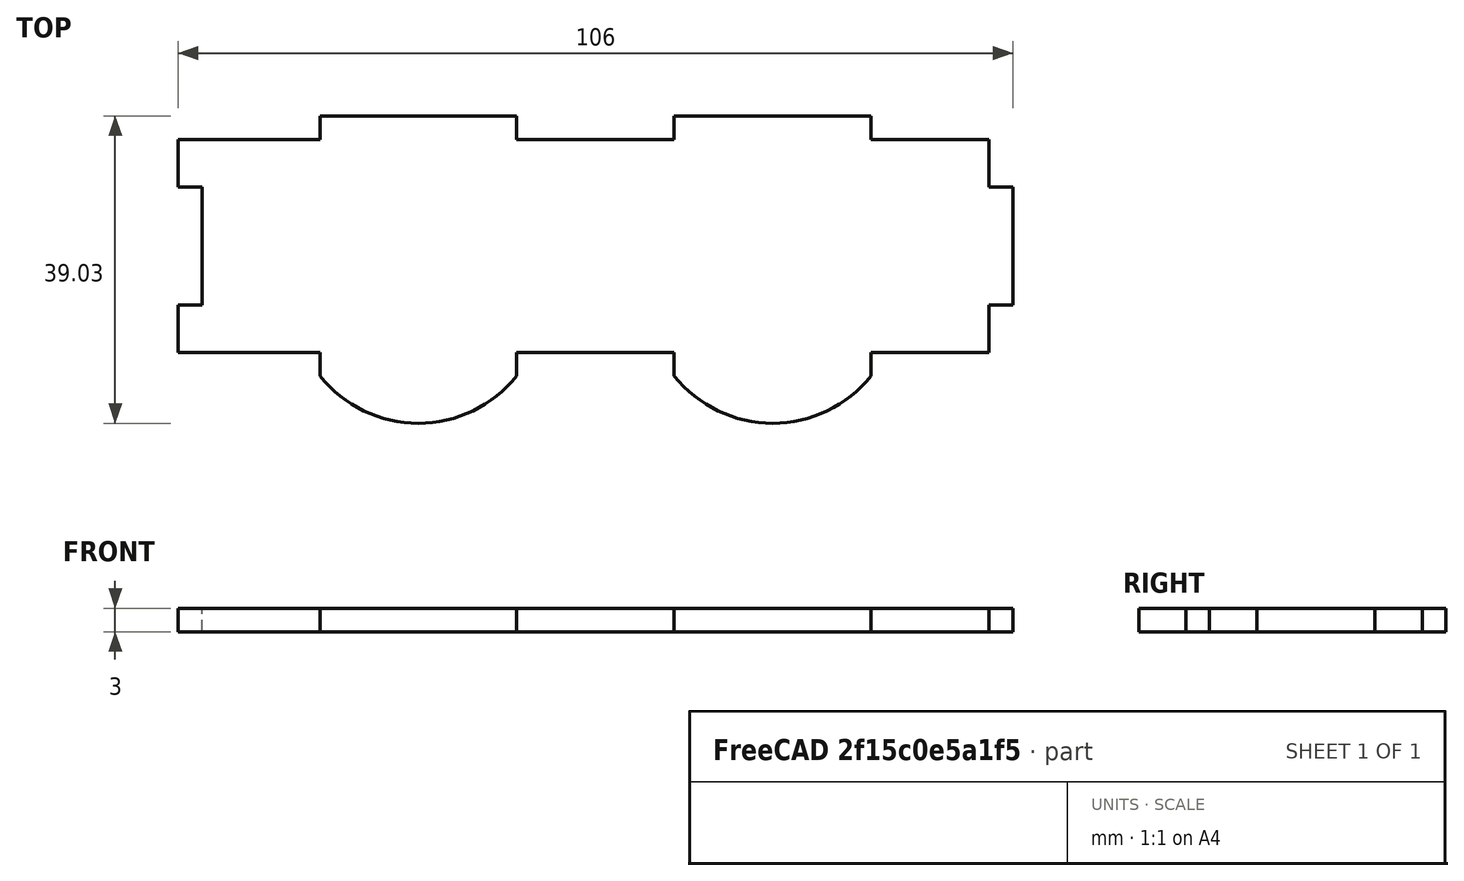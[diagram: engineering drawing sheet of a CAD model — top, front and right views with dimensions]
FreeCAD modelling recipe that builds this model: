
FCSTD DOCUMENT  (FreeCAD 0.19R24267 +99 (Git))
Label: side1
License: All rights reserved
LicenseURL: http://en.wikipedia.org/wiki/All_rights_reserved
objects: App::Part×1, Sketcher::SketchObject×1, Part::Extrusion×1
note: 2 computed .brp shape members not serialized (recipe doc carries the construction recipe); baked Part::Feature solids carry a one-line shape summary decoded from their .brp

FEATURE [App::Part] Part
  Origin = -> Origin
FEATURE [Sketcher::SketchObject] Sketch
  FullyConstrained = false
  sketch-geometry (48):
    g0: LineSegment StartX=0 StartY=0 StartZ=0 EndX=100 EndY=0 EndZ=0
    g1: LineSegment StartX=100 StartY=0 StartZ=0 EndX=100 EndY=1.6 EndZ=0
    g2: LineSegment StartX=100 StartY=1.6 StartZ=0 EndX=0 EndY=1.6 EndZ=0
    g3: LineSegment StartX=0 StartY=1.6 StartZ=0 EndX=0 EndY=0 EndZ=0
    g4: LineSegment StartX=0 StartY=-6.37 StartZ=0 EndX=100 EndY=-6.37 EndZ=0
    g5: LineSegment StartX=100 StartY=-6.37 StartZ=0 EndX=100 EndY=20.66 EndZ=0
    g6: LineSegment StartX=100 StartY=20.66 StartZ=0 EndX=0 EndY=20.66 EndZ=0
    g7: LineSegment StartX=0 StartY=20.66 StartZ=0 EndX=0 EndY=-6.37 EndZ=0
    g8: LineSegment StartX=15 StartY=-6.37 StartZ=0 EndX=40 EndY=-6.37 EndZ=0
    g9: LineSegment StartX=40 StartY=-6.37 StartZ=0 EndX=40 EndY=-9.37 EndZ=0
    g10: LineSegment StartX=40 StartY=-9.37 StartZ=0 EndX=15 EndY=-9.37 EndZ=0
    g11: LineSegment StartX=15 StartY=-9.37 StartZ=0 EndX=15 EndY=-6.37 EndZ=0
    g12: LineSegment StartX=60 StartY=-6.37 StartZ=0 EndX=85 EndY=-6.37 EndZ=0
    g13: LineSegment StartX=85 StartY=-6.37 StartZ=0 EndX=85 EndY=-9.37 EndZ=0
    g14: LineSegment StartX=85 StartY=-9.37 StartZ=0 EndX=60 EndY=-9.37 EndZ=0
    g15: LineSegment StartX=60 StartY=-9.37 StartZ=0 EndX=60 EndY=-6.37 EndZ=0
    g16: LineSegment StartX=15 StartY=20.66 StartZ=0 EndX=40 EndY=20.66 EndZ=0
    g17: LineSegment StartX=40 StartY=20.66 StartZ=0 EndX=40 EndY=23.66 EndZ=0
    g18: LineSegment StartX=40 StartY=23.66 StartZ=0 EndX=15 EndY=23.66 EndZ=0
    g19: LineSegment StartX=15 StartY=23.66 StartZ=0 EndX=15 EndY=20.66 EndZ=0
    g20: LineSegment StartX=60 StartY=20.66 StartZ=0 EndX=85 EndY=20.66 EndZ=0
    g21: LineSegment StartX=85 StartY=20.66 StartZ=0 EndX=85 EndY=23.66 EndZ=0
    g22: LineSegment StartX=85 StartY=23.66 StartZ=0 EndX=60 EndY=23.66 EndZ=0
    g23: LineSegment StartX=60 StartY=23.66 StartZ=0 EndX=60 EndY=20.66 EndZ=0
    g24: LineSegment StartX=100 StartY=14.66 StartZ=0 EndX=103 EndY=14.66 EndZ=0
    g25: LineSegment StartX=103 StartY=14.66 StartZ=0 EndX=103 EndY=-0.34 EndZ=0
    g26: LineSegment StartX=103 StartY=-0.34 StartZ=0 EndX=100 EndY=-0.34 EndZ=0
    g27: LineSegment StartX=100 StartY=-0.34 StartZ=0 EndX=100 EndY=14.66 EndZ=0
    g28: LineSegment StartX=0 StartY=-0.34 StartZ=0 EndX=0 EndY=14.66 EndZ=0
    g29: LineSegment StartX=0 StartY=20.66 StartZ=0 EndX=15 EndY=20.66 EndZ=0
    g30: LineSegment StartX=40 StartY=20.66 StartZ=0 EndX=60 EndY=20.66 EndZ=0
    g31: LineSegment StartX=85 StartY=20.66 StartZ=0 EndX=100 EndY=20.66 EndZ=0
    g32: LineSegment StartX=100 StartY=-0.34 StartZ=0 EndX=100 EndY=-6.37 EndZ=0
    g33: LineSegment StartX=100 StartY=-6.37 StartZ=0 EndX=85 EndY=-6.37 EndZ=0
    g34: LineSegment StartX=60 StartY=-6.37 StartZ=0 EndX=40 EndY=-6.37 EndZ=0
    g35: LineSegment StartX=15 StartY=-6.37 StartZ=0 EndX=0 EndY=-6.37 EndZ=0
    g36: LineSegment StartX=100 StartY=20.66 StartZ=0 EndX=100 EndY=14.66 EndZ=0
    g37: ArcOfCircle CenterX=27.5 CenterY=0.650833 CenterZ=0 NormalX=0 NormalY=0 NormalZ=1 AngleXU=0 Radius=16.0208 StartAngle=3.81735 EndAngle=5.60743
    g38: GeomPoint X=27.5 Y=-15.37 Z=0
    g39: ArcOfCircle CenterX=72.5 CenterY=0.650833 CenterZ=0 NormalX=0 NormalY=0 NormalZ=1 AngleXU=0 Radius=16.0208 StartAngle=3.81735 EndAngle=5.60743
    g40: GeomPoint X=72.5 Y=-15.37 Z=0
    g41: LineSegment StartX=0 StartY=14.66 StartZ=0 EndX=-3 EndY=14.66 EndZ=0
    g42: LineSegment StartX=-3 StartY=-0.34 StartZ=0 EndX=0 EndY=-0.34 EndZ=0
    g43: LineSegment StartX=-3 StartY=-0.34 StartZ=0 EndX=-3 EndY=-6.37 EndZ=0
    g44: LineSegment StartX=-3 StartY=-6.37 StartZ=0 EndX=0 EndY=-6.37 EndZ=0
    g45: LineSegment StartX=-3 StartY=14.66 StartZ=0 EndX=-3 EndY=20.66 EndZ=0
    g46: LineSegment StartX=-3 StartY=20.66 StartZ=0 EndX=0 EndY=20.66 EndZ=0
    g47: LineSegment StartX=0 StartY=14.66 StartZ=0 EndX=0 EndY=-0.34 EndZ=0
  constraints (129):
    c: Coincident(g0,g1)
    c: Coincident(g1,g2)
    c: Coincident(g2,g3)
    c: Coincident(g3,g0)
    c: Horizontal(g0)
    c: Horizontal(g2)
    c: Vertical(g1)
    c: Vertical(g3)
    c: Coincident(g0,g-1)
    c: DistanceX(g2,g2) = 100
    c: DistanceY(g3,g3) = 1.6
    c: Coincident(g4,g5)
    c: Coincident(g5,g6)
    c: Coincident(g6,g7)
    c: Coincident(g7,g4)
    c: Horizontal(g4)
    c: Horizontal(g6)
    c: Vertical(g5)
    c: Vertical(g7)
    c: PointOnObject(g4,g-2)
    c: Equal(g6,g2)
    c: DistanceY(g2,g6) = 19.06
    c: DistanceY(g4,g-1) = 6.37
    c: Coincident(g8,g9)
    c: Coincident(g9,g10)
    c: Coincident(g10,g11)
    c: Coincident(g11,g8)
    c: Horizontal(g8)
    c: Horizontal(g10)
    c: Vertical(g9)
    c: Vertical(g11)
    c: PointOnObject(g8,g4)
    c: Coincident(g12,g13)
    c: Coincident(g13,g14)
    c: Coincident(g14,g15)
    c: Coincident(g15,g12)
    c: Horizontal(g12)
    c: Horizontal(g14)
    c: Vertical(g13)
    c: Vertical(g15)
    c: PointOnObject(g12,g4)
    c: Coincident(g16,g17)
    c: Coincident(g17,g18)
    c: Coincident(g18,g19)
    c: Coincident(g19,g16)
    c: Horizontal(g16)
    c: Horizontal(g18)
    c: Vertical(g17)
    c: Vertical(g19)
    c: PointOnObject(g16,g6)
    c: Coincident(g20,g21)
    c: Coincident(g21,g22)
    c: Coincident(g22,g23)
    c: Coincident(g23,g20)
    c: Horizontal(g20)
    c: Horizontal(g22)
    c: Vertical(g21)
    c: Vertical(g23)
    c: PointOnObject(g20,g6)
    c: Coincident(g24,g25)
    c: Coincident(g25,g26)
    c: Coincident(g26,g27)
    c: Coincident(g27,g24)
    c: Horizontal(g24)
    c: Horizontal(g26)
    c: Vertical(g25)
    c: Vertical(g27)
    c: PointOnObject(g24,g5)
    c: Vertical(g28)
    c: PointOnObject(g28,g7)
    c: Equal(g18,g22)
    c: Equal(g14,g10)
    c: DistanceX(g18,g18) = 25
    c: Equal(g11,g15)
    c: Equal(g15,g23)
    c: Equal(g23,g24)
    c: DistanceY(g23,g23) = 3
    c: DistanceX(g6,g18) = 15
    c: DistanceX(g21,g5) = 15
    c: DistanceX(g13,g4) = 15
    c: DistanceX(g4,g10) = 15
    c: Equal(g14,g22)
    c: DistanceY(g25,g25) = 15
    c: DistanceY(g24,g5) = 6
    c: Coincident(g29,g16)
    c: Coincident(g30,g16)
    c: Coincident(g30,g20)
    c: Coincident(g31,g20)
    c: Coincident(g31,g5)
    c: Coincident(g32,g26)
    c: Coincident(g32,g4)
    c: Coincident(g33,g32)
    c: Coincident(g33,g12)
    c: Coincident(g34,g12)
    c: Coincident(g34,g8)
    c: Coincident(g35,g8)
    c: Coincident(g35,g4)
    c: Coincident(g36,g31)
    c: Coincident(g36,g24)
    c: Coincident(g37,g9)
    c: Coincident(g37,g10)
    c: PointOnObject(g38,g37)
    c: DistanceY(g38,g9) = 6
    c: DistanceX(g38,g9) = 12.5
    c: Coincident(g39,g14)
    c: Coincident(g39,g13)
    c: PointOnObject(g40,g39)
    c: DistanceX(g40,g13) = 12.5
    c: DistanceY(g40,g13) = 6
    c: Coincident(g41,g28)
    c: Horizontal(g41)
    c: PointOnObject(g42,g7)
    c: Horizontal(g42)
    c: DistanceY(g42,g41) = 15
    c: DistanceX(g41,g41) = 3
    c: Horizontal(g41,g24)
    c: Vertical(g43)
    c: Coincident(g44,g43)
    c: Coincident(g44,g35)
    c: Horizontal(g44)
    c: Coincident(g45,g41)
    c: Vertical(g45)
    c: Coincident(g46,g29)
    c: Horizontal(g46)
    c: Horizontal(g29,g19)
    c: Coincident(g47,g41)
    c: Coincident(g47,g42)
    c: DistanceY(g45,g45) = 6
    c: Equal(g43,g32)
FEATURE [Part::Extrusion] Extrude
  Base = -> Sketch
  Dir = (0,0,1)
  DirMode = 2
  FaceMakerClass = Part::FaceMakerBullseye
  LengthFwd = 3
  LengthRev = 0
  Solid = true
  Symmetric = false
